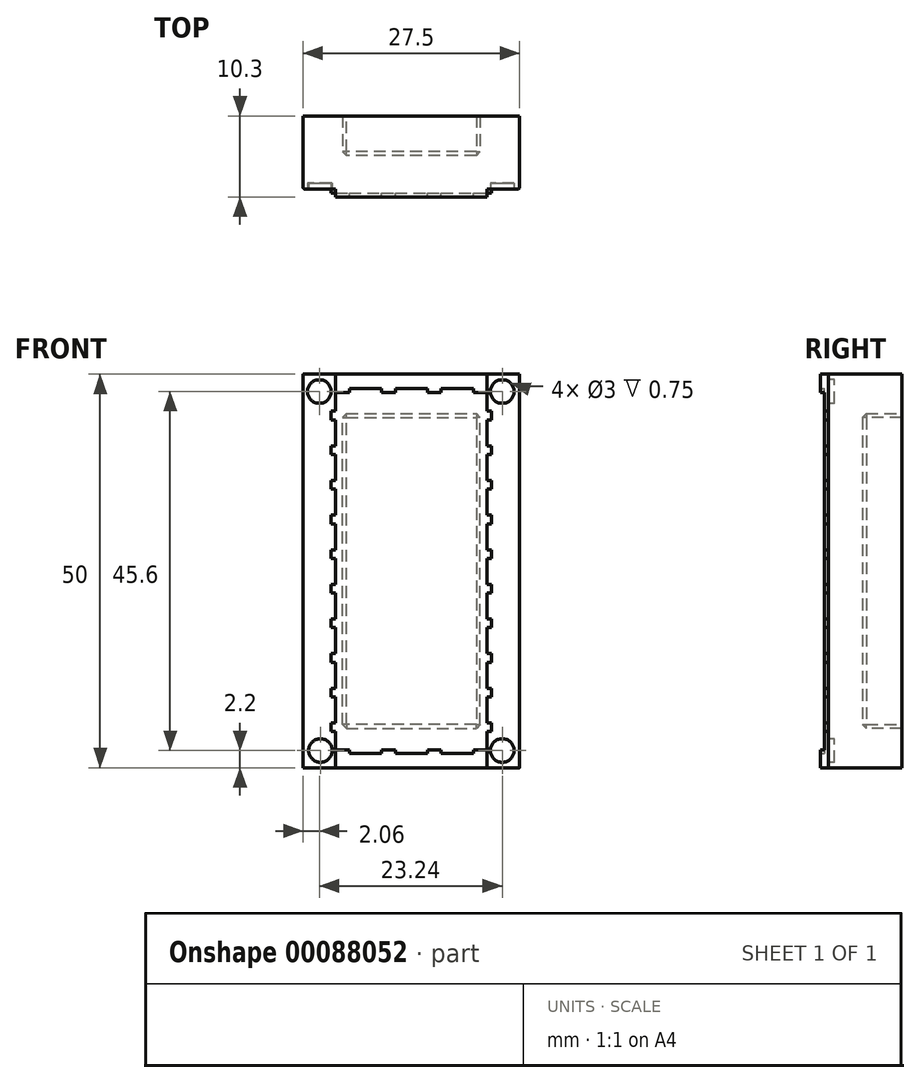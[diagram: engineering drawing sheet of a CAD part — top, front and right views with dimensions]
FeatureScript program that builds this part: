
annotation { "Feature Type Name" : "Feature", "Feature Type Description" : "" }
export const myFeature = defineFeature(function(context is Context, id is Id, definition is map)
    precondition{}
    {
        {
            var Q0;
            Q0=qCreatedBy(makeId("Front.planeOp"),FACE);
            var sketch = newSketch(context, id + "F0", { "sketchPlane" : qUnion([Q0])});
            skLineSegment(sketch, "E0.bottom", {"start": v(0, 0) * mm, "end": v(27.5, 0) * mm});
            skLineSegment(sketch, "E0.top", {"start": v(0, 50) * mm, "end": v(27.5, 50) * mm});
            skLineSegment(sketch, "E0.left", {"start": v(0, 0) * mm, "end": v(0, 50) * mm});
            skLineSegment(sketch, "E0.right", {"start": v(27.5, 0) * mm, "end": v(27.5, 50) * mm});
            skSolve(sketch);
        }
        {
            var Q0;
            Q0 = qSketchRegion(id + "F0", true);
            extrude(context, id + "F1", {"entities" : qUnion([Q0]), "depth" : 9.3 * mm});
        }
        {
            var Q0;
            Q0=makeQuery(id+"F1.opExtrude","CAP_FACE",FACE,{"disambiguationData":[OSD([sQuery(id+"F0.wireOp",EDGE,"E0.bottom"),sQuery(id+"F0.wireOp",EDGE,"E0.top"),sQuery(id+"F0.wireOp",EDGE,"E0.left"),sQuery(id+"F0.wireOp",EDGE,"E0.right")])],"isStart":false});
            var sketch = newSketch(context, id + "F2", { "sketchPlane" : qUnion([Q0])});
            skLineSegment(sketch, "E1", {"start": v(4.12, 50) * mm, "end": v(4.12, 45.3) * mm});
            skLineSegment(sketch, "E2", {"start": v(4.12, 45.3) * mm, "end": v(3.58, 45.3) * mm});
            skLineSegment(sketch, "E3", {"start": v(3.58, 45.3) * mm, "end": v(3.58, 44.2) * mm});
            skLineSegment(sketch, "E4", {"start": v(3.58, 44.2) * mm, "end": v(4.12, 44.2) * mm});
            skLineSegment(sketch, "E5", {"start": v(4.12, 44.2) * mm, "end": v(4.12, 40.9) * mm});
            skLineSegment(sketch, "E6", {"start": v(4.12, 40.9) * mm, "end": v(3.58, 40.9) * mm});
            skLineSegment(sketch, "E7", {"start": v(3.58, 40.9) * mm, "end": v(3.58, 39.8) * mm});
            skLineSegment(sketch, "E8", {"start": v(3.58, 39.8) * mm, "end": v(4.12, 39.8) * mm});
            skLineSegment(sketch, "E9", {"start": v(4.12, 39.8) * mm, "end": v(4.12, 36.5) * mm});
            skLineSegment(sketch, "E10", {"start": v(4.12, 36.5) * mm, "end": v(3.58, 36.5) * mm});
            skLineSegment(sketch, "E11", {"start": v(3.58, 36.5) * mm, "end": v(3.58, 35.4) * mm});
            skLineSegment(sketch, "E12", {"start": v(3.58, 35.4) * mm, "end": v(4.12, 35.4) * mm});
            skLineSegment(sketch, "E13", {"start": v(4.12, 35.4) * mm, "end": v(4.12, 32.1) * mm});
            skLineSegment(sketch, "E14", {"start": v(4.12, 32.1) * mm, "end": v(3.58, 32.1) * mm});
            skLineSegment(sketch, "E15", {"start": v(3.58, 32.1) * mm, "end": v(3.58, 31) * mm});
            skLineSegment(sketch, "E16", {"start": v(3.58, 31) * mm, "end": v(4.12, 31) * mm});
            skLineSegment(sketch, "E17", {"start": v(4.12, 31) * mm, "end": v(4.12, 27.7) * mm});
            skLineSegment(sketch, "E18", {"start": v(4.12, 27.7) * mm, "end": v(3.58, 27.7) * mm});
            skLineSegment(sketch, "E19", {"start": v(3.58, 27.7) * mm, "end": v(3.58, 26.6) * mm});
            skLineSegment(sketch, "E20", {"start": v(3.58, 26.6) * mm, "end": v(4.12, 26.6) * mm});
            skLineSegment(sketch, "E21", {"start": v(4.12, 26.6) * mm, "end": v(4.12, 23.3) * mm});
            skLineSegment(sketch, "E22", {"start": v(4.12, 23.3) * mm, "end": v(3.58, 23.3) * mm});
            skLineSegment(sketch, "E23", {"start": v(3.58, 23.3) * mm, "end": v(3.58, 22.2) * mm});
            skLineSegment(sketch, "E24", {"start": v(3.58, 22.2) * mm, "end": v(4.12, 22.2) * mm});
            skLineSegment(sketch, "E25", {"start": v(4.12, 22.2) * mm, "end": v(4.12, 18.9) * mm});
            skLineSegment(sketch, "E26", {"start": v(4.12, 18.9) * mm, "end": v(3.58, 18.9) * mm});
            skLineSegment(sketch, "E27", {"start": v(3.58, 18.9) * mm, "end": v(3.58, 17.8) * mm});
            skLineSegment(sketch, "E28", {"start": v(3.58, 17.8) * mm, "end": v(4.12, 17.8) * mm});
            skLineSegment(sketch, "E29", {"start": v(4.12, 17.8) * mm, "end": v(4.12, 14.5) * mm});
            skLineSegment(sketch, "E30", {"start": v(4.12, 14.5) * mm, "end": v(3.58, 14.5) * mm});
            skLineSegment(sketch, "E31", {"start": v(3.58, 14.5) * mm, "end": v(3.58, 13.4) * mm});
            skLineSegment(sketch, "E32", {"start": v(3.58, 13.4) * mm, "end": v(4.12, 13.4) * mm});
            skLineSegment(sketch, "E33", {"start": v(4.12, 13.4) * mm, "end": v(4.12, 10.1) * mm});
            skLineSegment(sketch, "E34", {"start": v(4.12, 10.1) * mm, "end": v(3.58, 10.1) * mm});
            skLineSegment(sketch, "E35", {"start": v(3.58, 10.1) * mm, "end": v(3.58, 9) * mm});
            skLineSegment(sketch, "E36", {"start": v(3.58, 9) * mm, "end": v(4.12, 9) * mm});
            skLineSegment(sketch, "E37", {"start": v(4.12, 9) * mm, "end": v(4.12, 5.7) * mm});
            skLineSegment(sketch, "E38", {"start": v(4.12, 5.7) * mm, "end": v(3.58, 5.7) * mm});
            skLineSegment(sketch, "E39", {"start": v(3.58, 5.7) * mm, "end": v(3.58, 4.6) * mm});
            skLineSegment(sketch, "E40", {"start": v(3.58, 4.6) * mm, "end": v(4.12, 4.6) * mm});
            skLineSegment(sketch, "E41", {"start": v(4.12, 4.6) * mm, "end": v(4.12, 0) * mm});
            skLineSegment(sketch, "E42", {"start": v(4.12, 50) * mm, "end": v(13.75, 50) * mm});
            skLineSegment(sketch, "E43", {"start": v(4.12, 0) * mm, "end": v(13.75, 0) * mm});
            skLineSegment(sketch, "E44", {"start": v(13.75, 50) * mm, "end": v(13.75, 0) * mm, "construction": true});
            skLineSegment(sketch, "E45.MirrorCS", {"start": v(23.92, 26.6) * mm, "end": v(23.38, 26.6) * mm});
            skLineSegment(sketch, "E46.MirrorCS", {"start": v(23.38, 23.3) * mm, "end": v(23.92, 23.3) * mm});
            skLineSegment(sketch, "E47.MirrorCS", {"start": v(23.38, 26.6) * mm, "end": v(23.38, 23.3) * mm});
            skLineSegment(sketch, "E48.MirrorCS", {"start": v(23.92, 35.4) * mm, "end": v(23.38, 35.4) * mm});
            skLineSegment(sketch, "E49.MirrorCS", {"start": v(23.92, 39.8) * mm, "end": v(23.38, 39.8) * mm});
            skLineSegment(sketch, "E50.MirrorCS", {"start": v(23.92, 31) * mm, "end": v(23.38, 31) * mm});
            skLineSegment(sketch, "E51.MirrorCS", {"start": v(23.38, 32.1) * mm, "end": v(23.92, 32.1) * mm});
            skLineSegment(sketch, "E52.MirrorCS", {"start": v(23.92, 27.7) * mm, "end": v(23.92, 26.6) * mm});
            skLineSegment(sketch, "E53.MirrorCS", {"start": v(23.92, 23.3) * mm, "end": v(23.92, 22.2) * mm});
            skLineSegment(sketch, "E54.MirrorCS", {"start": v(23.38, 10.1) * mm, "end": v(23.92, 10.1) * mm});
            skLineSegment(sketch, "E55.MirrorCS", {"start": v(23.38, 22.2) * mm, "end": v(23.38, 18.9) * mm});
            skLineSegment(sketch, "E56.MirrorCS", {"start": v(23.92, 22.2) * mm, "end": v(23.38, 22.2) * mm});
            skLineSegment(sketch, "E57.MirrorCS", {"start": v(23.92, 13.4) * mm, "end": v(23.38, 13.4) * mm});
            skLineSegment(sketch, "E58.MirrorCS", {"start": v(23.38, 18.9) * mm, "end": v(23.92, 18.9) * mm});
            skLineSegment(sketch, "E59.MirrorCS", {"start": v(23.38, 27.7) * mm, "end": v(23.92, 27.7) * mm});
            skLineSegment(sketch, "E60.MirrorCS", {"start": v(23.38, 14.5) * mm, "end": v(23.92, 14.5) * mm});
            skLineSegment(sketch, "E61.MirrorCS", {"start": v(23.38, 31) * mm, "end": v(23.38, 27.7) * mm});
            skLineSegment(sketch, "E62.MirrorCS", {"start": v(23.38, 35.4) * mm, "end": v(23.38, 32.1) * mm});
            skLineSegment(sketch, "E63.MirrorCS", {"start": v(23.92, 36.5) * mm, "end": v(23.92, 35.4) * mm});
            skLineSegment(sketch, "E64.MirrorCS", {"start": v(23.38, 36.5) * mm, "end": v(23.92, 36.5) * mm});
            skLineSegment(sketch, "E65.MirrorCS", {"start": v(23.38, 39.8) * mm, "end": v(23.38, 36.5) * mm});
            skLineSegment(sketch, "E66.MirrorCS", {"start": v(23.92, 9) * mm, "end": v(23.38, 9) * mm});
            skLineSegment(sketch, "E67.MirrorCS", {"start": v(23.38, 40.9) * mm, "end": v(23.92, 40.9) * mm});
            skLineSegment(sketch, "E68.MirrorCS", {"start": v(23.92, 32.1) * mm, "end": v(23.92, 31) * mm});
            skLineSegment(sketch, "E69.MirrorCS", {"start": v(23.92, 18.9) * mm, "end": v(23.92, 17.8) * mm});
            skLineSegment(sketch, "E70.MirrorCS", {"start": v(23.92, 10.1) * mm, "end": v(23.92, 9) * mm});
            skLineSegment(sketch, "E71.MirrorCS", {"start": v(23.38, 17.8) * mm, "end": v(23.38, 14.5) * mm});
            skLineSegment(sketch, "E72.MirrorCS", {"start": v(23.92, 17.8) * mm, "end": v(23.38, 17.8) * mm});
            skLineSegment(sketch, "E73.MirrorCS", {"start": v(23.38, 13.4) * mm, "end": v(23.38, 10.1) * mm});
            skLineSegment(sketch, "E74.MirrorCS", {"start": v(23.92, 14.5) * mm, "end": v(23.92, 13.4) * mm});
            skLineSegment(sketch, "E75.MirrorCS", {"start": v(23.38, 9) * mm, "end": v(23.38, 5.7) * mm});
            skLineSegment(sketch, "E76.MirrorCS", {"start": v(23.92, 40.9) * mm, "end": v(23.92, 39.8) * mm});
            skLineSegment(sketch, "E77.MirrorCS", {"start": v(23.38, 5.7) * mm, "end": v(23.92, 5.7) * mm});
            skLineSegment(sketch, "E78.MirrorCS", {"start": v(23.92, 44.2) * mm, "end": v(23.38, 44.2) * mm});
            skLineSegment(sketch, "E79.MirrorCS", {"start": v(23.38, 45.3) * mm, "end": v(23.92, 45.3) * mm});
            skLineSegment(sketch, "E80.MirrorCS", {"start": v(23.92, 4.6) * mm, "end": v(23.38, 4.6) * mm});
            skLineSegment(sketch, "E81.MirrorCS", {"start": v(23.92, 5.7) * mm, "end": v(23.92, 4.6) * mm});
            skLineSegment(sketch, "E82.MirrorCS", {"start": v(23.38, 44.2) * mm, "end": v(23.38, 40.9) * mm});
            skLineSegment(sketch, "E83.MirrorCS", {"start": v(23.92, 45.3) * mm, "end": v(23.92, 44.2) * mm});
            skLineSegment(sketch, "E84.MirrorCS", {"start": v(23.38, 0) * mm, "end": v(13.75, 0) * mm});
            skLineSegment(sketch, "E85.MirrorCS", {"start": v(23.38, 50) * mm, "end": v(13.75, 50) * mm});
            skLineSegment(sketch, "E86.MirrorCS", {"start": v(23.38, 4.6) * mm, "end": v(23.38, 0) * mm});
            skLineSegment(sketch, "E87.MirrorCS", {"start": v(23.38, 50) * mm, "end": v(23.38, 45.3) * mm});
            skSolve(sketch);
        }
        {
            var Q0;
            Q0 = qSketchRegion(id + "F2", true);
            extrude(context, id + "F3", {"entities" : qUnion([Q0]), "operationType" : NewBodyOperationType.ADD, "depth" : .5 * mm, "offsetDistance" : 25 * mm});
        }
        {
            var Q0;
            {var subQ0=sQuery(id+"F0.wireOp",EDGE,"E0.left");var subQ1=sQuery(id+"F0.wireOp",EDGE,"E0.top");var subQ2=sQuery(id+"F0.wireOp",EDGE,"E0.bottom");Q0=makeQuery(id+"F3.boolean.opBoolean","SPLIT",FACE,{"disambiguationData":[TD([makeQuery(id+"F1.opExtrude","SWEPT_FACE",FACE,{"disambiguationData":[OSD([subQ0])]})])],"derivedFrom":makeQuery(id+"F1.opExtrude","CAP_FACE",FACE,{"disambiguationData":[OSD([subQ2,subQ1,subQ0,sQuery(id+"F0.wireOp",EDGE,"E0.right")])],"isStart":false})});}
            var sketch = newSketch(context, id + "F4", { "sketchPlane" : qUnion([Q0])});
            skCircle(sketch, "E88", {"center": v(2.2, 2.2) * mm, "radius": 1.5 * mm});
            skCircle(sketch, "E89", {"center": v(25.3, 2.2) * mm, "radius": 1.5 * mm});
            skCircle(sketch, "E90", {"center": v(2.06, 47.8) * mm, "radius": 1.5 * mm});
            skPoint(sketch, "E90.centerSnap0", {"position": v(2.06, 50) * mm});
            skCircle(sketch, "E91", {"center": v(25.3, 47.8) * mm, "radius": 1.5 * mm});
            skSolve(sketch);
        }
        {
            var Q0;
            Q0 = qSketchRegion(id + "F4", true);
            extrude(context, id + "F5", {"entities" : qUnion([Q0]), "operationType" : NewBodyOperationType.REMOVE, "oppositeDirection" : true, "depth" : .75 * mm, "offsetDistance" : 25 * mm});
        }
        {
            var Q0;
            Q0=makeQuery(id+"F1.opExtrude","CAP_EDGE",EDGE,{"disambiguationData":[OSD([sQuery(id+"F0.wireOp",EDGE,"E0.left")])],"isStart":false});
            var Q1;
            Q1=makeQuery(id+"F1.opExtrude","CAP_EDGE",EDGE,{"disambiguationData":[OSD([sQuery(id+"F0.wireOp",EDGE,"E0.right")])],"isStart":false});
            fillet(context, id + "F6", {"entities" : qUnion([Q0, Q1]), "radius" : .25 * mm, "tangentPropagation" : true, "allowEdgeOverflow" : false});
        }
        {
            var Q0;
            Q0=makeQuery(id+"F3.opExtrude","CAP_FACE",FACE,{"disambiguationData":[OSD([sQuery(id+"F2.wireOp",EDGE,"E1"),sQuery(id+"F2.wireOp",EDGE,"E2"),sQuery(id+"F2.wireOp",EDGE,"E3"),sQuery(id+"F2.wireOp",EDGE,"E4"),sQuery(id+"F2.wireOp",EDGE,"E5"),sQuery(id+"F2.wireOp",EDGE,"E6"),sQuery(id+"F2.wireOp",EDGE,"E7"),sQuery(id+"F2.wireOp",EDGE,"E8"),sQuery(id+"F2.wireOp",EDGE,"E9"),sQuery(id+"F2.wireOp",EDGE,"E10"),sQuery(id+"F2.wireOp",EDGE,"E11"),sQuery(id+"F2.wireOp",EDGE,"E12"),sQuery(id+"F2.wireOp",EDGE,"E13"),sQuery(id+"F2.wireOp",EDGE,"E14"),sQuery(id+"F2.wireOp",EDGE,"E15"),sQuery(id+"F2.wireOp",EDGE,"E16"),sQuery(id+"F2.wireOp",EDGE,"E17"),sQuery(id+"F2.wireOp",EDGE,"E18"),sQuery(id+"F2.wireOp",EDGE,"E19"),sQuery(id+"F2.wireOp",EDGE,"E20"),sQuery(id+"F2.wireOp",EDGE,"E21"),sQuery(id+"F2.wireOp",EDGE,"E22"),sQuery(id+"F2.wireOp",EDGE,"E23"),sQuery(id+"F2.wireOp",EDGE,"E24"),sQuery(id+"F2.wireOp",EDGE,"E25"),sQuery(id+"F2.wireOp",EDGE,"E26"),sQuery(id+"F2.wireOp",EDGE,"E27"),sQuery(id+"F2.wireOp",EDGE,"E28"),sQuery(id+"F2.wireOp",EDGE,"E29"),sQuery(id+"F2.wireOp",EDGE,"E30"),sQuery(id+"F2.wireOp",EDGE,"E31"),sQuery(id+"F2.wireOp",EDGE,"E32"),sQuery(id+"F2.wireOp",EDGE,"E33"),sQuery(id+"F2.wireOp",EDGE,"E34"),sQuery(id+"F2.wireOp",EDGE,"E35"),sQuery(id+"F2.wireOp",EDGE,"E36"),sQuery(id+"F2.wireOp",EDGE,"E37"),sQuery(id+"F2.wireOp",EDGE,"E38"),sQuery(id+"F2.wireOp",EDGE,"E39"),sQuery(id+"F2.wireOp",EDGE,"E40"),sQuery(id+"F2.wireOp",EDGE,"E41"),sQuery(id+"F2.wireOp",EDGE,"E42"),sQuery(id+"F2.wireOp",EDGE,"E43"),sQuery(id+"F2.wireOp",EDGE,"E45.MirrorCS"),sQuery(id+"F2.wireOp",EDGE,"E46.MirrorCS"),sQuery(id+"F2.wireOp",EDGE,"E47.MirrorCS"),sQuery(id+"F2.wireOp",EDGE,"E48.MirrorCS"),sQuery(id+"F2.wireOp",EDGE,"E49.MirrorCS"),sQuery(id+"F2.wireOp",EDGE,"E50.MirrorCS"),sQuery(id+"F2.wireOp",EDGE,"E51.MirrorCS"),sQuery(id+"F2.wireOp",EDGE,"E52.MirrorCS"),sQuery(id+"F2.wireOp",EDGE,"E53.MirrorCS"),sQuery(id+"F2.wireOp",EDGE,"E54.MirrorCS"),sQuery(id+"F2.wireOp",EDGE,"E55.MirrorCS"),sQuery(id+"F2.wireOp",EDGE,"E56.MirrorCS"),sQuery(id+"F2.wireOp",EDGE,"E57.MirrorCS"),sQuery(id+"F2.wireOp",EDGE,"E58.MirrorCS"),sQuery(id+"F2.wireOp",EDGE,"E59.MirrorCS"),sQuery(id+"F2.wireOp",EDGE,"E60.MirrorCS"),sQuery(id+"F2.wireOp",EDGE,"E61.MirrorCS"),sQuery(id+"F2.wireOp",EDGE,"E62.MirrorCS"),sQuery(id+"F2.wireOp",EDGE,"E63.MirrorCS"),sQuery(id+"F2.wireOp",EDGE,"E64.MirrorCS"),sQuery(id+"F2.wireOp",EDGE,"E65.MirrorCS"),sQuery(id+"F2.wireOp",EDGE,"E66.MirrorCS"),sQuery(id+"F2.wireOp",EDGE,"E67.MirrorCS"),sQuery(id+"F2.wireOp",EDGE,"E68.MirrorCS"),sQuery(id+"F2.wireOp",EDGE,"E69.MirrorCS"),sQuery(id+"F2.wireOp",EDGE,"E70.MirrorCS"),sQuery(id+"F2.wireOp",EDGE,"E71.MirrorCS"),sQuery(id+"F2.wireOp",EDGE,"E72.MirrorCS"),sQuery(id+"F2.wireOp",EDGE,"E73.MirrorCS"),sQuery(id+"F2.wireOp",EDGE,"E74.MirrorCS"),sQuery(id+"F2.wireOp",EDGE,"E75.MirrorCS"),sQuery(id+"F2.wireOp",EDGE,"E76.MirrorCS"),sQuery(id+"F2.wireOp",EDGE,"E77.MirrorCS"),sQuery(id+"F2.wireOp",EDGE,"E78.MirrorCS"),sQuery(id+"F2.wireOp",EDGE,"E79.MirrorCS"),sQuery(id+"F2.wireOp",EDGE,"E80.MirrorCS"),sQuery(id+"F2.wireOp",EDGE,"E81.MirrorCS"),sQuery(id+"F2.wireOp",EDGE,"E82.MirrorCS"),sQuery(id+"F2.wireOp",EDGE,"E83.MirrorCS"),sQuery(id+"F2.wireOp",EDGE,"E84.MirrorCS"),sQuery(id+"F2.wireOp",EDGE,"E85.MirrorCS"),sQuery(id+"F2.wireOp",EDGE,"E86.MirrorCS"),sQuery(id+"F2.wireOp",EDGE,"E87.MirrorCS")])],"isStart":false});
            var sketch = newSketch(context, id + "F7", { "sketchPlane" : qUnion([Q0])});
            skLineSegment(sketch, "E92.bottom", {"start": v(4.12, 50) * mm, "end": v(23.38, 50) * mm});
            skLineSegment(sketch, "E92.top", {"start": v(5.87, 48.2) * mm, "end": v(9.97, 48.2) * mm});
            skLineSegment(sketch, "E92.left", {"start": v(4.12, 50) * mm, "end": v(4.12, 48.2) * mm});
            skLineSegment(sketch, "E92.right", {"start": v(23.38, 50) * mm, "end": v(23.38, 48.2) * mm});
            skLineSegment(sketch, "E93", {"start": v(13.75, 50) * mm, "end": v(13.75, 0) * mm, "construction": true});
            skLineSegment(sketch, "E94", {"start": v(13.75, 25) * mm, "end": v(20.57, 25) * mm, "construction": true});
            skLineSegment(sketch, "E95.0", {"start": v(4.12, 47.7) * mm, "end": v(5.87, 47.7) * mm});
            skLineSegment(sketch, "E96", {"start": v(4.12, 47.7) * mm, "end": v(4.12, 48.2) * mm});
            skLineSegment(sketch, "E97", {"start": v(23.38, 47.7) * mm, "end": v(23.38, 48.2) * mm});
            skLineSegment(sketch, "E98.0", {"start": v(5.87, 47.7) * mm, "end": v(5.87, 48.2) * mm});
            skLineSegment(sketch, "E99.0", {"start": v(21.63, 47.7) * mm, "end": v(21.63, 48.2) * mm});
            skLineSegment(sketch, "E100.0", {"start": v(9.97, 47.7) * mm, "end": v(9.97, 48.2) * mm});
            skLineSegment(sketch, "E101.0", {"start": v(17.53, 47.7) * mm, "end": v(17.53, 48.2) * mm});
            skLineSegment(sketch, "E102.0", {"start": v(11.72, 47.7) * mm, "end": v(11.72, 48.2) * mm});
            skLineSegment(sketch, "E103.0", {"start": v(15.78, 47.7) * mm, "end": v(15.78, 48.2) * mm});
            skLineSegment(sketch, "E104.trimOffspring", {"start": v(15.78, 47.7) * mm, "end": v(17.53, 47.7) * mm});
            skLineSegment(sketch, "E105.trimOffspring", {"start": v(17.53, 48.2) * mm, "end": v(21.63, 48.2) * mm});
            skLineSegment(sketch, "E106.trimOffspring", {"start": v(21.63, 47.7) * mm, "end": v(23.38, 47.7) * mm});
            skLineSegment(sketch, "E107.trimOffspring", {"start": v(11.72, 48.2) * mm, "end": v(15.78, 48.2) * mm});
            skLineSegment(sketch, "E108.trimOffspring", {"start": v(9.97, 47.7) * mm, "end": v(11.72, 47.7) * mm});
            skLineSegment(sketch, "E109.MirrorCS", {"start": v(21.63, 2.3) * mm, "end": v(21.63, 1.8) * mm});
            skLineSegment(sketch, "E110.MirrorCS", {"start": v(4.12, 2.3) * mm, "end": v(5.87, 2.3) * mm});
            skLineSegment(sketch, "E111.MirrorCS", {"start": v(23.38, 2.3) * mm, "end": v(23.38, 1.8) * mm});
            skLineSegment(sketch, "E112.MirrorCS", {"start": v(4.12, 0) * mm, "end": v(4.12, 1.8) * mm});
            skLineSegment(sketch, "E113.MirrorCS", {"start": v(21.63, 2.3) * mm, "end": v(23.38, 2.3) * mm});
            skLineSegment(sketch, "E114.MirrorCS", {"start": v(9.97, 2.3) * mm, "end": v(11.72, 2.3) * mm});
            skLineSegment(sketch, "E115.MirrorCS", {"start": v(4.12, 2.3) * mm, "end": v(4.12, 1.8) * mm});
            skLineSegment(sketch, "E116.MirrorCS", {"start": v(23.38, 0) * mm, "end": v(23.38, 1.8) * mm});
            skLineSegment(sketch, "E117.MirrorCS", {"start": v(5.87, 2.3) * mm, "end": v(5.87, 1.8) * mm});
            skLineSegment(sketch, "E118.MirrorCS", {"start": v(11.72, 2.3) * mm, "end": v(11.72, 1.8) * mm});
            skLineSegment(sketch, "E119.MirrorCS", {"start": v(17.53, 2.3) * mm, "end": v(17.53, 1.8) * mm});
            skLineSegment(sketch, "E120.MirrorCS", {"start": v(15.78, 2.3) * mm, "end": v(15.78, 1.8) * mm});
            skLineSegment(sketch, "E121.MirrorCS", {"start": v(15.78, 2.3) * mm, "end": v(17.53, 2.3) * mm});
            skLineSegment(sketch, "E122.MirrorCS", {"start": v(9.97, 2.3) * mm, "end": v(9.97, 1.8) * mm});
            skLineSegment(sketch, "E123.MirrorCS", {"start": v(11.72, 1.8) * mm, "end": v(15.78, 1.8) * mm});
            skLineSegment(sketch, "E124.MirrorCS", {"start": v(5.87, 1.8) * mm, "end": v(9.97, 1.8) * mm});
            skLineSegment(sketch, "E125.MirrorCS", {"start": v(4.12, 0) * mm, "end": v(23.38, 0) * mm});
            skLineSegment(sketch, "E126.MirrorCS", {"start": v(17.53, 1.8) * mm, "end": v(21.63, 1.8) * mm});
            skSolve(sketch);
        }
        {
            var Q0;
            Q0 = qSketchRegion(id + "F7", true);
            extrude(context, id + "F8", {"entities" : qUnion([Q0]), "operationType" : NewBodyOperationType.ADD, "depth" : .5 * mm, "offsetDistance" : 25 * mm});
        }
        {
            var Q0;
            Q0=makeQuery(id+"F0.imprint","IMPRINT",FACE,{"disambiguationData":[TD([[makeQuery(id+"F0.imprint","IMPRINT",EDGE,{"derivedFrom":sQuery(id+"F0.wireOp",EDGE,"E0.bottom")}),1.0]])]});
            var sketch = newSketch(context, id + "F9", { "sketchPlane" : qUnion([Q0])});
            skLineSegment(sketch, "E127.0", {"start": v(5, 45) * mm, "end": v(22.5, 45) * mm});
            skLineSegment(sketch, "E128.0", {"start": v(22.5, 5) * mm, "end": v(22.5, 45) * mm});
            skLineSegment(sketch, "E129.0", {"start": v(5, 5) * mm, "end": v(22.5, 5) * mm});
            skLineSegment(sketch, "E130.0", {"start": v(5, 5) * mm, "end": v(5, 45) * mm});
            skSolve(sketch);
        }
        {
            var Q0;
            Q0 = qSketchRegion(id + "F9", true);
            extrude(context, id + "F10", {"entities" : qUnion([Q0]), "operationType" : NewBodyOperationType.REMOVE, "depth" : 5 * mm, "offsetDistance" : 25 * mm});
        }
        {
            var Q0;
            Q0=makeQuery(id+"F10.boolean.opBoolean","COPY",EDGE,{"derivedFrom":makeQuery(id+"F10.opExtrude","SWEPT_EDGE",EDGE,{"disambiguationData":[OSD([sQuery(id+"F9.wireOp",EDGE,"E127.0"),sQuery(id+"F9.wireOp",EDGE,"E130.0")])]})});
            var Q1;
            Q1=makeQuery(id+"F10.boolean.opBoolean","COPY",EDGE,{"derivedFrom":makeQuery(id+"F10.opExtrude","CAP_EDGE",EDGE,{"disambiguationData":[OSD([sQuery(id+"F9.wireOp",EDGE,"E127.0")])],"isStart":false})});
            var Q2;
            Q2=makeQuery(id+"F10.boolean.opBoolean","COPY",EDGE,{"derivedFrom":makeQuery(id+"F10.opExtrude","CAP_EDGE",EDGE,{"disambiguationData":[OSD([sQuery(id+"F9.wireOp",EDGE,"E130.0")])],"isStart":false})});
            var Q3;
            Q3=makeQuery(id+"F10.boolean.opBoolean","COPY",EDGE,{"derivedFrom":makeQuery(id+"F10.opExtrude","CAP_EDGE",EDGE,{"disambiguationData":[OSD([sQuery(id+"F9.wireOp",EDGE,"E128.0")])],"isStart":false})});
            var Q4;
            Q4=makeQuery(id+"F10.boolean.opBoolean","COPY",EDGE,{"derivedFrom":makeQuery(id+"F10.opExtrude","SWEPT_EDGE",EDGE,{"disambiguationData":[OSD([sQuery(id+"F9.wireOp",EDGE,"E129.0"),sQuery(id+"F9.wireOp",EDGE,"E130.0")])]})});
            var Q5;
            Q5=makeQuery(id+"F10.boolean.opBoolean","COPY",EDGE,{"derivedFrom":makeQuery(id+"F10.opExtrude","CAP_EDGE",EDGE,{"disambiguationData":[OSD([sQuery(id+"F9.wireOp",EDGE,"E129.0")])],"isStart":false})});
            var Q6;
            Q6=makeQuery(id+"F10.boolean.opBoolean","COPY",EDGE,{"derivedFrom":makeQuery(id+"F10.opExtrude","SWEPT_EDGE",EDGE,{"disambiguationData":[OSD([sQuery(id+"F9.wireOp",EDGE,"E128.0"),sQuery(id+"F9.wireOp",EDGE,"E129.0")])]})});
            var Q7;
            Q7=makeQuery(id+"F10.boolean.opBoolean","COPY",EDGE,{"derivedFrom":makeQuery(id+"F10.opExtrude","CAP_EDGE",EDGE,{"disambiguationData":[OSD([sQuery(id+"F9.wireOp",EDGE,"E129.0")])],"isStart":true})});
            var Q8;
            Q8=makeQuery(id+"F10.boolean.opBoolean","COPY",EDGE,{"derivedFrom":makeQuery(id+"F10.opExtrude","SWEPT_EDGE",EDGE,{"disambiguationData":[OSD([sQuery(id+"F9.wireOp",EDGE,"E127.0"),sQuery(id+"F9.wireOp",EDGE,"E128.0")])]})});
            chamfer(context, id + "F11", {"entities" : qUnion([Q0, Q1, Q2, Q3, Q4, Q5, Q6, Q7, Q8]), "width" : .5 * mm, "tangentPropagation" : true});
        }
    });
